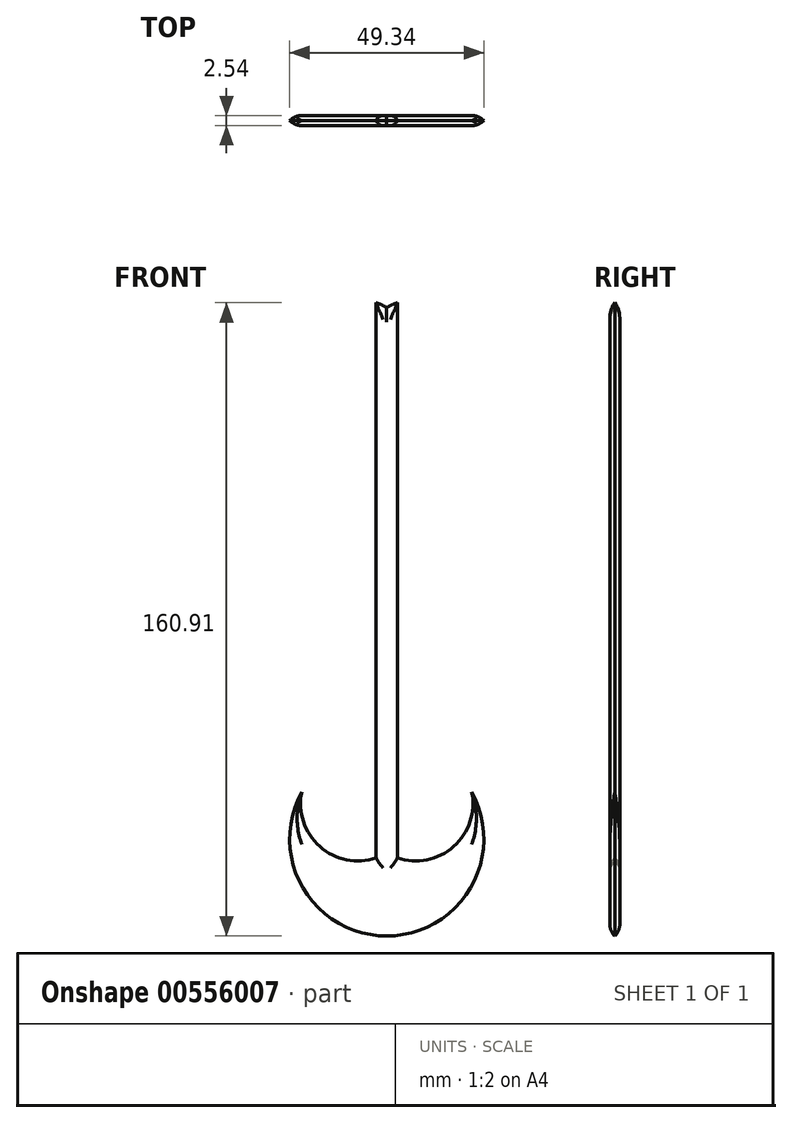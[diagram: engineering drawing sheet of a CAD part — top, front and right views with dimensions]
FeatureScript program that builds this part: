
annotation { "Feature Type Name" : "Feature", "Feature Type Description" : "" }
export const myFeature = defineFeature(function(context is Context, id is Id, definition is map)
    precondition{}
    {
        {
            var Q0;
            Q0=qCreatedBy(makeId("Front.planeOp"),FACE);
            var sketch = newSketch(context, id + "F0", { "sketchPlane" : qUnion([Q0])});
            skLineSegment(sketch, "E0", {"start": v(0, 76.07) * mm, "end": v(0, -69.26) * mm});
            skArc(sketch, "E1", {"start": v(-21.58, -53.8) * mm, "mid": v(-15.85, -68.6) * mm, "end": v(0, -69.26) * mm});
            skArc(sketch, "E2.MirrorCS", {"start": v(21.58, -53.8) * mm, "mid": v(15.85, -68.6) * mm, "end": v(0, -69.26) * mm});
            skArc(sketch, "E3", {"start": v(-21.58, -53.8) * mm, "mid": v(0, -90.4) * mm, "end": v(21.58, -53.8) * mm});
            skArc(sketch, "E4.MirrorCS", {"start": v(-21.58, 53.8) * mm, "mid": v(-15.85, 68.6) * mm, "end": v(0, 69.26) * mm});
            skArc(sketch, "E5.MirrorCS", {"start": v(21.58, 53.8) * mm, "mid": v(15.85, 68.6) * mm, "end": v(0, 69.26) * mm});
            skArc(sketch, "E6.MirrorCS", {"start": v(-21.58, 53.8) * mm, "mid": v(0, 90.4) * mm, "end": v(21.58, 53.8) * mm});
            skLineSegment(sketch, "E7", {"start": v(-2.69, 70.51) * mm, "end": v(-2.69, -70.51) * mm});
            skLineSegment(sketch, "E8.MirrorCS", {"start": v(2.69, 70.51) * mm, "end": v(2.69, -70.51) * mm});
            skSolve(sketch);
        }
        {
            var Q0;
            {var subQ5=sQuery(id+"F0.wireOp",EDGE,"E8.MirrorCS");Q0=makeQuery(id+"F0.imprint","IMPRINT",FACE,{"disambiguationData":[TD([[makeQuery(id+"F0.imprint","IMPRINT",EDGE,{"derivedFrom":subQ5}),-1.0]])]});}
            var Q1;
            {var subQ5=sQuery(id+"F0.wireOp",EDGE,"E7");Q1=makeQuery(id+"F0.imprint","IMPRINT",FACE,{"disambiguationData":[TD([[makeQuery(id+"F0.imprint","IMPRINT",EDGE,{"derivedFrom":subQ5}),1.0]])]});}
            var Q2;
            {var subQ4=sQuery(id+"F0.wireOp",EDGE,"E6.MirrorCS");Q2=makeQuery(id+"F0.imprint","IMPRINT",FACE,{"disambiguationData":[TD([[makeQuery(id+"F0.imprint","IMPRINT",EDGE,{"derivedFrom":subQ4}),-1.0]])]});}
            var Q3;
            {var subQ4=sQuery(id+"F0.wireOp",EDGE,"E3");Q3=makeQuery(id+"F0.imprint","IMPRINT",FACE,{"disambiguationData":[TD([[makeQuery(id+"F0.imprint","IMPRINT",EDGE,{"derivedFrom":subQ4}),1.0]])]});}
            extrude(context, id + "F1", {"entities" : qUnion([Q0, Q1, Q2, Q3]), "depth" : 1.27 * mm, "offsetDistance" : 25.4 * mm});
        }
        {
            var Q0;
            Q0=makeQuery(id+"F1.opExtrude","CAP_EDGE",EDGE,{"disambiguationData":[OSD([sQuery(id+"F0.wireOp",EDGE,"E6.MirrorCS")])],"isStart":false});
            var Q1;
            Q1=makeQuery(id+"F1.opExtrude","CAP_EDGE",EDGE,{"disambiguationData":[OSD([sQuery(id+"F0.wireOp",EDGE,"E5.MirrorCS")])],"isStart":false});
            var Q2;
            Q2=makeQuery(id+"F1.opExtrude","CAP_EDGE",EDGE,{"disambiguationData":[OSD([sQuery(id+"F0.wireOp",EDGE,"E4.MirrorCS")])],"isStart":false});
            var Q3;
            Q3=makeQuery(id+"F1.opExtrude","CAP_EDGE",EDGE,{"disambiguationData":[OSD([sQuery(id+"F0.wireOp",EDGE,"E1")])],"isStart":false});
            var Q4;
            Q4=makeQuery(id+"F1.opExtrude","CAP_EDGE",EDGE,{"disambiguationData":[OSD([sQuery(id+"F0.wireOp",EDGE,"E3")])],"isStart":false});
            var Q5;
            Q5=makeQuery(id+"F1.opExtrude","CAP_EDGE",EDGE,{"disambiguationData":[OSD([sQuery(id+"F0.wireOp",EDGE,"E2.MirrorCS")])],"isStart":false});
            fillet(context, id + "F2", {"entities" : qUnion([Q0, Q1, Q2, Q3, Q4, Q5]), "radius" : 4.3 * mm, "tangentPropagation" : true, "allowEdgeOverflow" : false});
        }
        {
            var Q0;
            Q0=makeQuery(id+"F1.opExtrude","CAP_EDGE",EDGE,{"disambiguationData":[OSD([sQuery(id+"F0.wireOp",EDGE,"E7")])],"isStart":false});
            var Q1;
            Q1=makeQuery(id+"F1.opExtrude","CAP_EDGE",EDGE,{"disambiguationData":[OSD([sQuery(id+"F0.wireOp",EDGE,"E8.MirrorCS")])],"isStart":false});
            fillet(context, id + "F3", {"entities" : qUnion([Q0, Q1]), "radius" : 1.84 * mm, "tangentPropagation" : true, "allowEdgeOverflow" : false});
        }
        {
            var Q0;
            Q0=makeQuery(id+"F1.opExtrude","SWEPT_BODY",BODY,{"disambiguationData":[OSD([sQuery(id+"F0.wireOp",EDGE,"E1"),sQuery(id+"F0.wireOp",EDGE,"E2.MirrorCS"),sQuery(id+"F0.wireOp",EDGE,"E3"),sQuery(id+"F0.wireOp",EDGE,"E4.MirrorCS"),sQuery(id+"F0.wireOp",EDGE,"E5.MirrorCS"),sQuery(id+"F0.wireOp",EDGE,"E6.MirrorCS"),sQuery(id+"F0.wireOp",EDGE,"E7"),sQuery(id+"F0.wireOp",EDGE,"E8.MirrorCS")])]});
            var Q1;
            Q1=qCreatedBy(makeId("Front.planeOp"),FACE);
            mirror(context, id + "F4", {"operationType" : NewBodyOperationType.ADD, "entities" : qUnion([Q0]), "mirrorPlane" : qUnion([Q1])});
        }
    });
